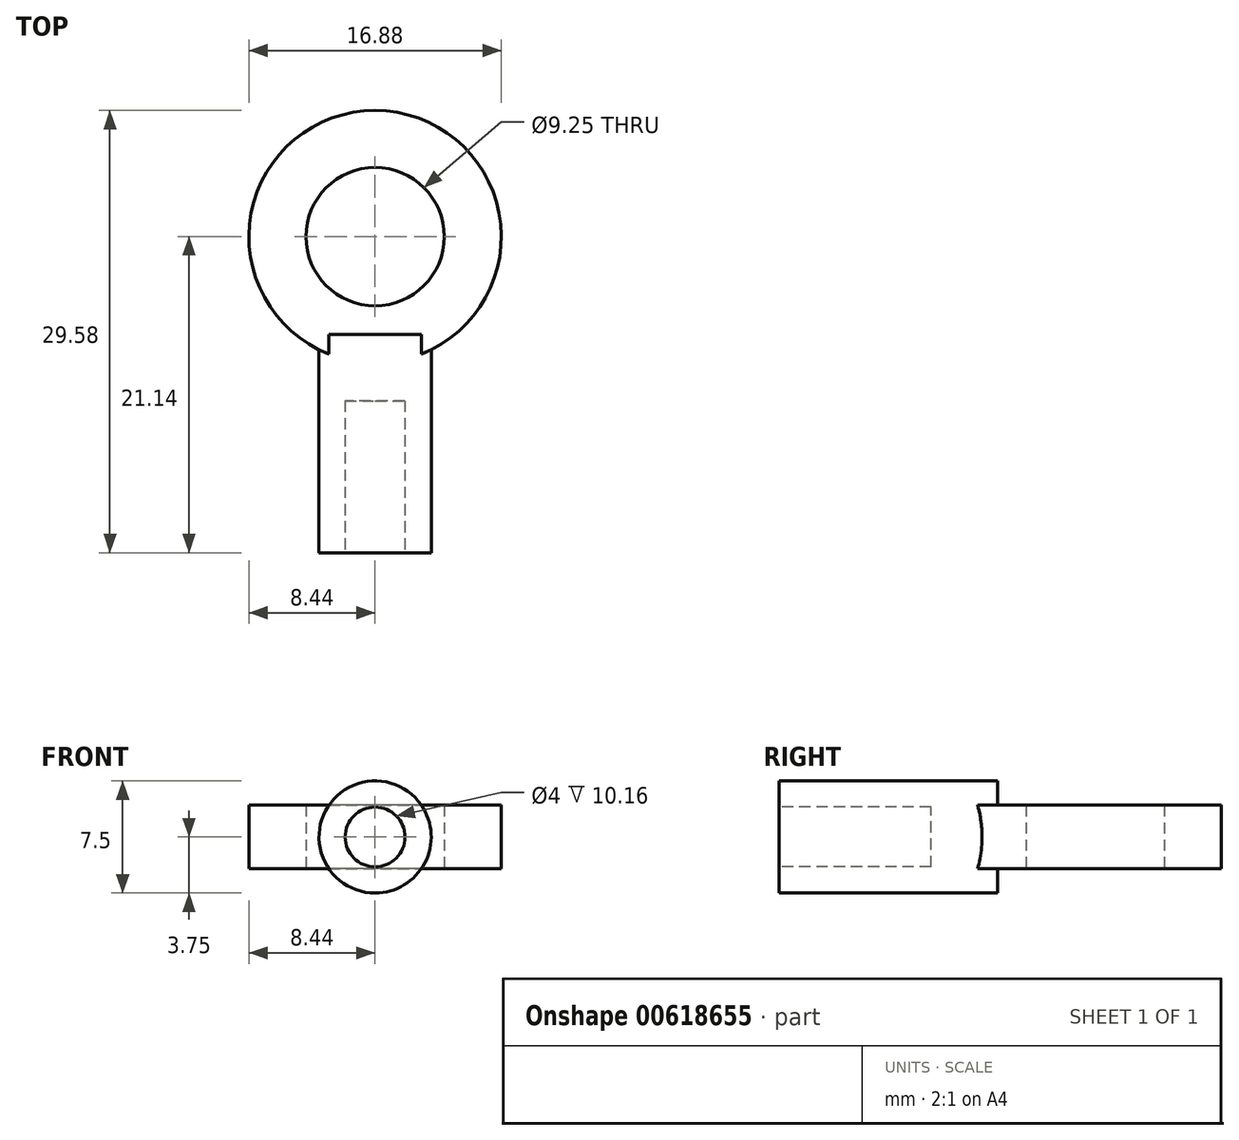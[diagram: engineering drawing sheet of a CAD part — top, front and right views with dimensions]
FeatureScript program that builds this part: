
annotation { "Feature Type Name" : "Feature", "Feature Type Description" : "" }
export const myFeature = defineFeature(function(context is Context, id is Id, definition is map)
    precondition{}
    {
        {
            var Q0;
            Q0=qCreatedBy(makeId("Top.planeOp"),FACE);
            var sketch = newSketch(context, id + "F0", { "sketchPlane" : qUnion([Q0])});
            skCircle(sketch, "E0", {"center": v(0, 0) * mm, "radius": 4.63 * mm});
            skCircle(sketch, "E1", {"center": v(0, 0) * mm, "radius": 8.44 * mm});
            skSolve(sketch);
        }
        {
            var Q0;
            Q0 = qSketchRegion(id + "F0", true);
            extrude(context, id + "F1", {"entities" : qUnion([Q0]), "endBound" : BoundingType.SYMMETRIC, "depth" : 4.25 * mm, "offsetDistance" : 25.4 * mm});
        }
        {
            var Q0;
            Q0=qCreatedBy(makeId("Front.planeOp"),FACE);
            cPlane(context, id + "F2", {"entities" : qUnion([Q0]), "cplaneType" : CPlaneType.OFFSET, "offset" : (9.25 * mm / 2) + (3.8 * mm / 2), "width" : 152.4 * mm, "height" : 152.4 * mm});
        }
        {
            var Q0;
            Q0=qCreatedBy(id+"F2.planeOp",FACE);
            var sketch = newSketch(context, id + "F3", { "sketchPlane" : qUnion([Q0])});
            skCircle(sketch, "E2", {"center": v(0, 0) * mm, "radius": 3.75 * mm});
            skCircle(sketch, "E3", {"center": v(0, 0) * mm, "radius": 2 * mm});
            skSolve(sketch);
        }
        {
            var Q0;
            Q0=makeQuery(id+"F3.imprint","IMPRINT",FACE,{"disambiguationData":[TD([[makeQuery(id+"F3.imprint","IMPRINT",EDGE,{"derivedFrom":sQuery(id+"F3.wireOp",EDGE,"E3")}),1.0]])]});
            var Q1;
            Q1=makeQuery(id+"F3.imprint","IMPRINT",FACE,{"disambiguationData":[TD([[makeQuery(id+"F3.imprint","IMPRINT",EDGE,{"derivedFrom":sQuery(id+"F3.wireOp",EDGE,"E2")}),1.0]])]});
            extrude(context, id + "F4", {"entities" : qUnion([Q0, Q1]), "operationType" : NewBodyOperationType.ADD, "depth" : 14.6 * mm, "offsetDistance" : 25.4 * mm});
        }
        {
            var Q0;
            Q0=makeQuery(id+"F4.opExtrude","CAP_FACE",FACE,{"disambiguationData":[OSD([sQuery(id+"F3.wireOp",EDGE,"E2")])],"isStart":false});
            var sketch = newSketch(context, id + "F5", { "sketchPlane" : qUnion([Q0])});
            skCircle(sketch, "E4.0.0", {"center": v(0, 0) * mm, "radius": 3.75 * mm, "construction": true});
            skCircle(sketch, "E5", {"center": v(0, 0) * mm, "radius": 2 * mm});
            skSolve(sketch);
        }
        {
            var Q0;
            Q0 = qSketchRegion(id + "F5", true);
            extrude(context, id + "F6", {"entities" : qUnion([Q0]), "operationType" : NewBodyOperationType.REMOVE, "oppositeDirection" : true, "depth" : 10.16 * mm, "offsetDistance" : 25.4 * mm});
        }
    });
